# Revit family: LELW
name_source: partatom
category: Lighting Fixtures
units: mm (PartAtom-declared; Revit-internal decimal feet)

## family parameters
Always vertical = Yes
Cut with Voids When Loaded = No
Host = Wall
Light Source = Yes
OmniClass Number = 23.80.70.00
OmniClass Title = Lighting
Part Type = Normal
Room Calculation Point = No
Round Connector Dimension = Use Diameter
Shared = No

## types (5) — shared parameters
Assembly Code = D5020200
Color Filter = 16777215
Description = Specification-Grade ADA Surface Mount LED Luminarie
Dimming Lamp Color Temperature Shift = <None>
Housing Finish = Metal - Viscor - White
Lamp = LED
Lens Finish = Acrylic - Viscor - Frosted Extruded Micro-Grooved
Manufacturer = VISIONEERING by VISCOR
Model = LELW
Tilt Angle = -180.00°
URL = https://www.viscor.com
Voltage = 120 V
Width = 0' - 8 1/16"

## per-type parameters (varying)
| type | Apparent Load | Emit from Line Length | Lamp Wattage | Length | Photometric Web File |
| LELW24-LED840K020LUNV | 16 VA | 1' - 11 1/32" | 16 VA | 1' - 11 1/32" | LELW24-LED840K020LUNV.ies |
| LELW24-LED840K041LUNV | 32 VA | 1' - 11 1/32" | 32 VA | 1' - 11 1/32" | LELW24-LED840K041LUNV.ies |
| LELW48-LED840K053LUNV | 39 VA | 3' - 9 1/32" | 39 VA | 3' - 9 1/32" | LELW48-LED840K053LUNV.ies |
| LELW48-LED840K082LUNV | 64 VA | 3' - 9 1/32" | 64 VA | 3' - 9 1/32" | LELW48-LED840K082LUNV.ies |
| LELW48-LED840K041LUNV | 32 VA | 3' - 9 1/32" | 32 VA | 3' - 9 1/32" | LELW48-LED840K041LUNV.ies |

## geometry (parser evidence)
native form markers: Sweep x2
no freeform markers — native parametric forms only
